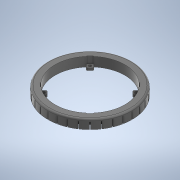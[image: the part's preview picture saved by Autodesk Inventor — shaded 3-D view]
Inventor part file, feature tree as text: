
AUTODESK INVENTOR PART (.ipt)
format: ipt  version: 2020 (Build 240168000, 168)  size: 1,241,600 bytes
history: native  units: mm
features: extrude x9, sketch x8, projected_geometry x8, pattern_circular x5, fillet x4, other x1
ambient origin geometry x8: Origin, YZ Plane, XZ Plane, XY Plane, X Axis, Y Axis, Z Axis, Center Point
bodies: Body1 (feature_tree)
feature tree (35):
  other  "Твердое тело1"
  sketch  "Эскиз1"
  extrude  "Выдавливание1"  Depth=88.0mm
  extrude  "Выдавливание2"  Depth=5.7mm
  pattern_circular  "Круговой массив1"  [2 undecoded]
  extrude  "Выдавливание3"  Depth=5.4mm
  fillet  "Сопряжение1"  Radius=98.0mm
  extrude  "Выдавливание4"  Depth=84.0mm
  pattern_circular  "Круговой массив2"  [2 undecoded]
  fillet  "Сопряжение2"  Radius=98.0mm
  extrude  "Выдавливание5"  Depth=84.0mm
  pattern_circular  "Круговой массив3"  [2 undecoded]
  extrude  "Выдавливание6"  Depth=10.0mm TaperAngle=0.0deg
  fillet  "Сопряжение3"  Radius=320.0mm
  sketch  "Эскиз6"
  extrude  "Выдавливание7"  Depth=2.0mm
  pattern_circular  "Круговой массив4"  [2 undecoded]
  extrude  "Выдавливание8"  Depth=1.0mm TaperAngle=0.0deg
  extrude  "Выдавливание9"  Depth=2.0mm
  pattern_circular  "Круговой массив5"  [2 undecoded]
  fillet  "Сопряжение4"  Radius=320.0mm
  sketch  "Эскиз2"
  sketch  "Эскиз3"
  projected_geometry  "Спроецированная петля1"
  sketch  "Эскиз4"
  projected_geometry  "Спроецированная петля2"
  sketch  "Эскиз5"
  projected_geometry  "Спроецированная петля3"
  projected_geometry  "Спроецированная петля4"
  projected_geometry  "Спроецированная петля5"
  projected_geometry  "Спроецированная петля6"
  projected_geometry  "Спроецированная петля7"
  sketch  "Эскиз7"
  sketch  "Эскиз8"
  projected_geometry  "Спроецированная петля8"
note: 10 required parameter values undecoded (feature->parameter linkage not recoverable at this tier; creation-order binding heuristic only, values carry confidence <= 0.55)
